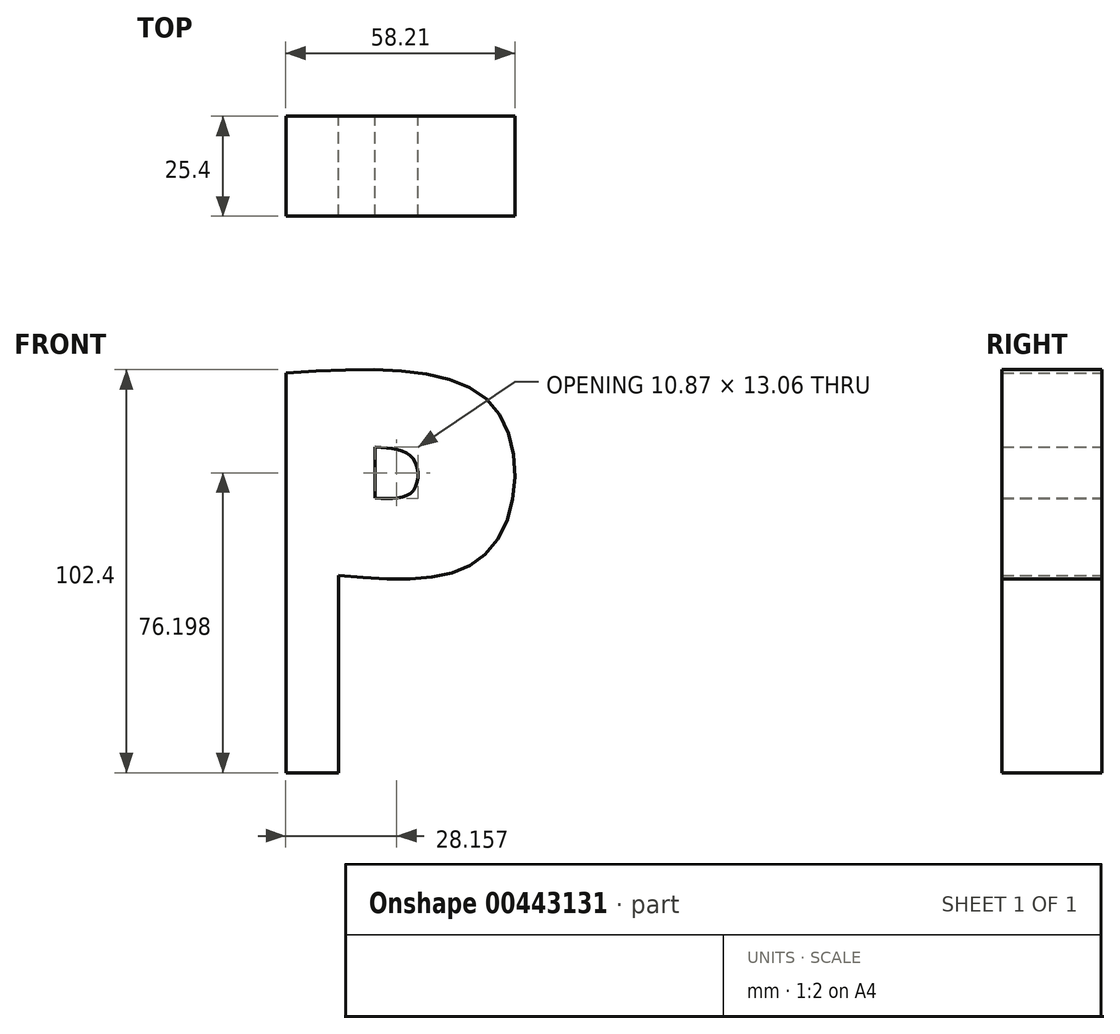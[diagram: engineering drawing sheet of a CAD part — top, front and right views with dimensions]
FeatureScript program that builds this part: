
annotation { "Feature Type Name" : "Feature", "Feature Type Description" : "" }
export const myFeature = defineFeature(function(context is Context, id is Id, definition is map)
    precondition{}
    {
        {
            var Q0;
            Q0=qCreatedBy(makeId("Front.planeOp"),FACE);
            var sketch = newSketch(context, id + "F0", { "sketchPlane" : qUnion([Q0])});
            skLineSegment(sketch, "E0", {"start": v(-39.45, 47.6) * mm, "end": v(-39.45, -54) * mm});
            skFitSpline(sketch, "E1", {"points": [v(-39.45, 47.6) * mm, v(13.7, 38.6) * mm, v(12.3, 2.52) * mm, v(-26.02, -3.92) * mm], "startDerivative": vector(176.1, 10.19) * mm, "endDerivative": vector(-142.76, 11.7) * mm});
            skLineSegment(sketch, "E2", {"start": v(-26.02, -3.92) * mm, "end": v(-26.02, -54) * mm});
            skLineSegment(sketch, "E3", {"start": v(-26.02, -54) * mm, "end": v(-39.45, -54) * mm});
            skLineSegment(sketch, "E4", {"start": v(-16.73, 28.74) * mm, "end": v(-16.73, 15.78) * mm});
            skPoint(sketch, "E5.1.internal.orphan", {"position": v(-7.13, 28.74) * mm});
            skFitSpline(sketch, "E6", {"points": [v(-16.73, 28.74) * mm, v(-7.13, 25.83) * mm, v(-7.13, 17.57) * mm, v(-16.73, 15.78) * mm], "startDerivative": vector(33.64, -2) * mm, "endDerivative": vector(-34.12, 1.77) * mm});
            skSolve(sketch);
        }
        {
            var Q0;
            Q0 = qSketchRegion(id + "F0", true);
            extrude(context, id + "F1", {"entities" : qUnion([Q0]), "depth" : 25.4 * mm});
        }
    });
